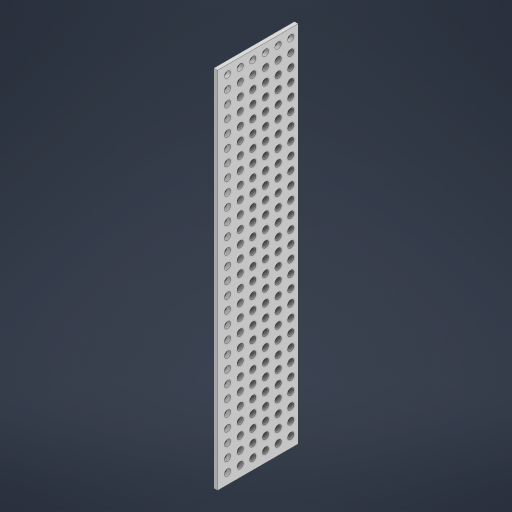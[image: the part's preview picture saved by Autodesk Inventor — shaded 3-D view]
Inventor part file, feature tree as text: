
AUTODESK INVENTOR PART (.ipt)
format: ipt  version: 2023 (Build 270158000, 158)  size: 344,576 bytes
history: native  units: mm
features: extrude x2, sketch x2, pattern_linear x1
ambient origin geometry x8: Origin, YZ Plane, XZ Plane, XY Plane, X Axis, Y Axis, Z Axis, Center Point
bodies: Solid1 (feature_tree)
feature tree (5):
  extrude  "Extrusion1"  Depth=288.0mm
  extrude  "Extrusion2"  Depth=10.0mm
  pattern_linear  "Rectangular Pattern1"  Spacing1=3.0mm  [1 undecoded]
  sketch  "Sketch1"  dims[d0=63.9mm d1=288.0mm]
  sketch  "Sketch2"  dims[d2=3.0mm d3=0.0mm d4=5.0mm d5=3.0mm d6=0.0mm d7=280.0mm d9=10.1mm d10=60.0mm d12=10.0mm]
note: 1 required parameter value undecoded (feature->parameter linkage not recoverable at this tier; creation-order binding heuristic only, values carry confidence <= 0.55)
